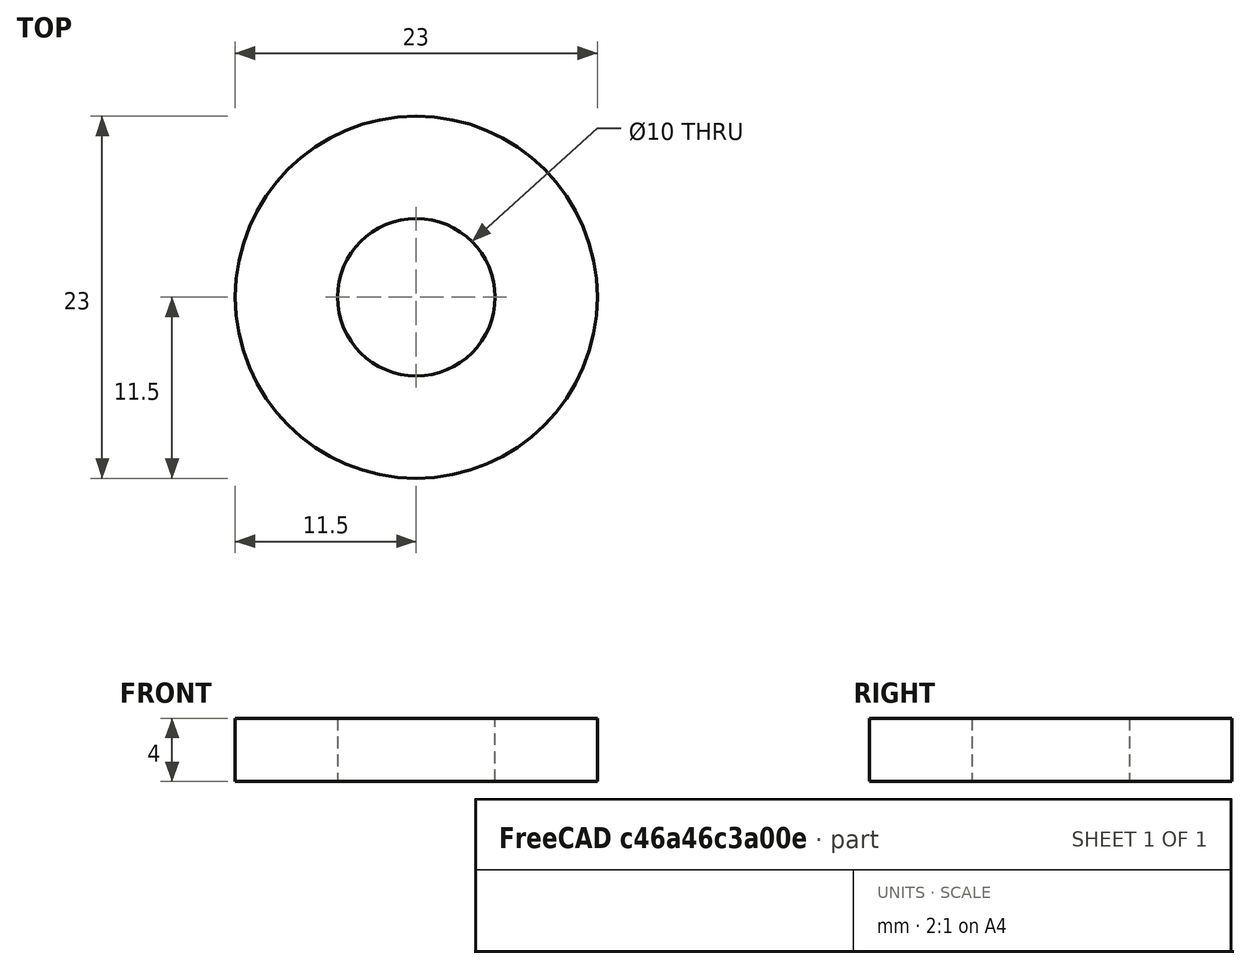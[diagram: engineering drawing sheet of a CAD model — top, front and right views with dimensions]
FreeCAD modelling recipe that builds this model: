
FCSTD DOCUMENT  (FreeCAD 0.19R24276 (Git))
Label: шайба
License: All rights reserved
LicenseURL: http://en.wikipedia.org/wiki/All_rights_reserved
objects: Sketcher::SketchObject×1, PartDesign::Pad×1, PartDesign::Body×1
note: 4 computed .brp shape members not serialized (recipe doc carries the construction recipe); baked Part::Feature solids carry a one-line shape summary decoded from their .brp

FEATURE [Sketcher::SketchObject] Sketch
  FullyConstrained = true
  MapMode = 5
  Support = -> [XY_Plane]
  sketch-geometry (2):
    g0: Circle CenterX=0 CenterY=0 CenterZ=0 NormalX=0 NormalY=0 NormalZ=1 AngleXU=0 Radius=11.5
    g1: Circle CenterX=0 CenterY=0 CenterZ=0 NormalX=0 NormalY=0 NormalZ=1 AngleXU=0 Radius=5
  constraints (4):
    c: Coincident(g0,g-1)
    c: Coincident(g1,g0)
    c: Radius(g0) = 11.5
    c: Radius(g1) = 5
FEATURE [PartDesign::Pad] Pad
  Direction = (1,1,1)
  Length = 4
  Length2 = 100
  Profile = -> Sketch
  Type = 0
FEATURE [PartDesign::Body] Body
  Group = -> [Sketch,Pad]
  Origin = -> Origin
  Tip = -> Pad
